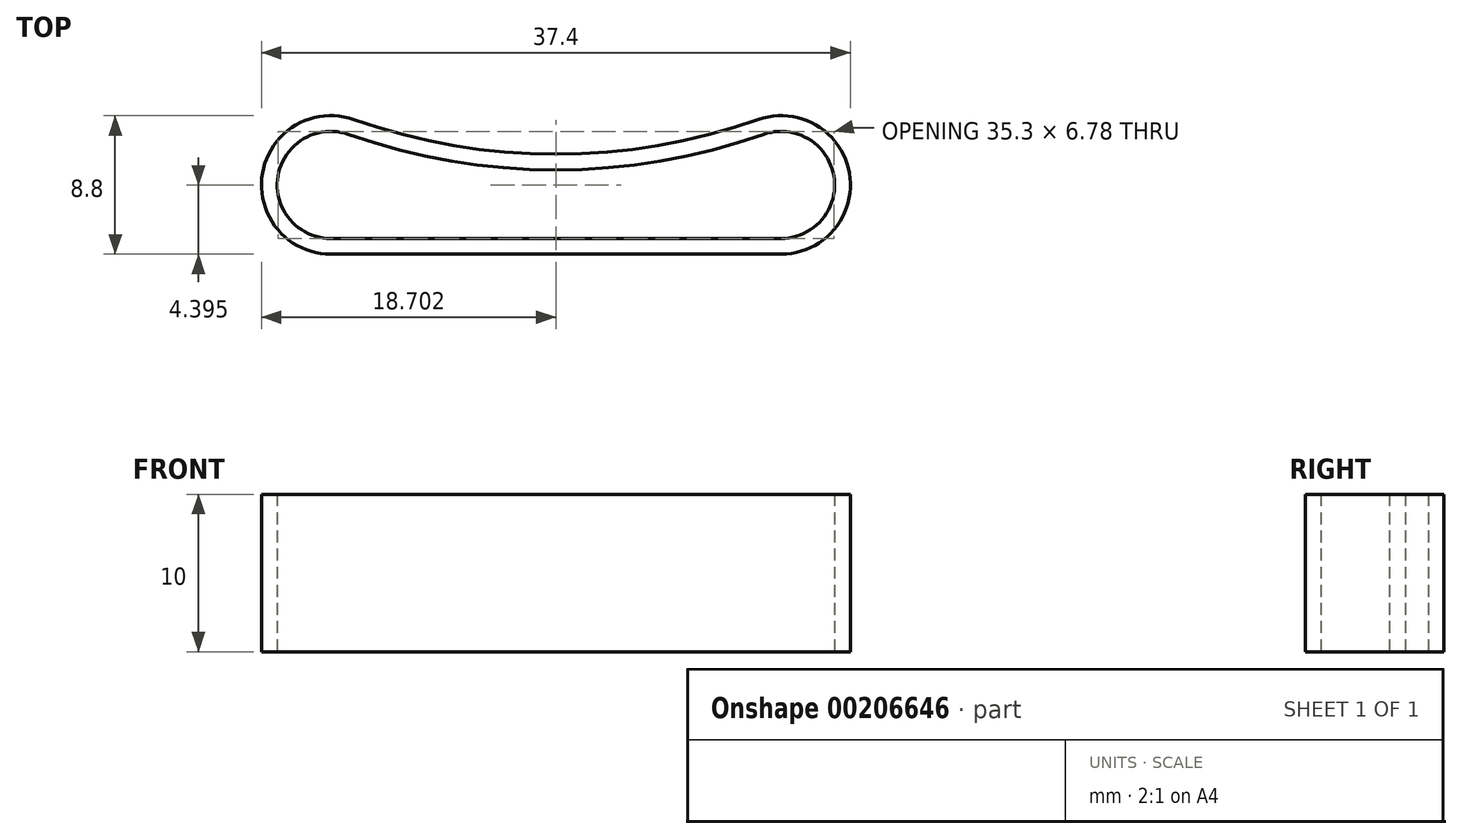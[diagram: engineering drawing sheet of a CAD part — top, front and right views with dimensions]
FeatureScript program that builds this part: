
annotation { "Feature Type Name" : "Feature", "Feature Type Description" : "" }
export const myFeature = defineFeature(function(context is Context, id is Id, definition is map)
    precondition{}
    {
        {
            var Q0;
            Q0=qCreatedBy(makeId("Top.planeOp"),FACE);
            var sketch = newSketch(context, id + "F0", { "sketchPlane" : qUnion([Q0])});
            skLineSegment(sketch, "E0.top", {"start": v(-142.05, -10.98) * mm, "end": v(-113.45, -10.98) * mm});
            skArc(sketch, "E1", {"start": v(-113.45, -10.98) * mm, "mid": v(-110.1, -7) * mm, "end": v(-114.58, -4.37) * mm});
            skArc(sketch, "E2", {"start": v(-140.92, -4.37) * mm, "mid": v(-145.4, -7) * mm, "end": v(-142.05, -10.98) * mm});
            skArc(sketch, "E3", {"start": v(-140.92, -4.37) * mm, "mid": v(-127.75, -6.63) * mm, "end": v(-114.58, -4.37) * mm});
            skPoint(sketch, "E4.start.orphan", {"position": v(-127.75, -10.98) * mm});
            skPoint(sketch, "E5.trimOffspring.end.orphan", {"position": v(-113.45, -4.18) * mm});
            skPoint(sketch, "E0.bottom.start.orphan", {"position": v(-142.05, -4.18) * mm});
            skArc(sketch, "E6.0", {"start": v(-140.58, -3.43) * mm, "mid": v(-127.75, -5.63) * mm, "end": v(-114.91, -3.43) * mm});
            skArc(sketch, "E6.1", {"start": v(-140.58, -3.43) * mm, "mid": v(-146.39, -6.83) * mm, "end": v(-142.05, -11.98) * mm});
            skLineSegment(sketch, "E6.2", {"start": v(-142.05, -11.98) * mm, "end": v(-113.45, -11.98) * mm});
            skArc(sketch, "E6.3", {"start": v(-113.45, -11.98) * mm, "mid": v(-109.11, -6.83) * mm, "end": v(-114.91, -3.43) * mm});
            skSolve(sketch);
        }
        {
            var Q0;
            Q0 = qSketchRegion(id + "F0", true);
            extrude(context, id + "F1", {"entities" : qUnion([Q0]), "depth" : 10 * mm});
        }
    });
